# Revit family: RG50_RG50S_CC32VA_CC32SVA_CC34VA
name_source: partatom
category: Specialty Equipment
revit_build: Autodesk Revit MEP 2012 (Build: 20110916_2132(x64)
units: mm (PartAtom-declared; Revit-internal decimal feet)

## types (5) — shared parameters
Apparent Power = 0 VA
Assembly Code = E1090320
Conn Conduit = Yes
Cycle = 50 Hz
Depth = 350 mm
Description = VEGETABLE PREPARATION MACHINE 2 KG/MINUTE
Elec Conn Connection Height = 50 mm  [stored 0.164042 ft]
FL Amps = 0 A
Height = 465 mm
Manufacturer = HALLDE
Max Overcurrent Protection = 10 A
Min Ckt Ampacity = 0 A
Phase = 1
URL = www.hallde.com
Volts = 230 V
Watts = 1000 W
Weight = 8 kg
Width = 285 mm

## type names (no varying parameters)
- RG-50
- RG-50S
- CC-32-VA
- CC-32S-VA
- CC-34-VA

note: column(s) folded — value = type name in every type: Model

note: [stored X ft] marks values corroborated as IEEE doubles in the binary element streams (Revit-internal decimal feet)

## geometry (parser evidence)
native form markers: Blend x12, Sweep x2
no freeform markers — native parametric forms only
